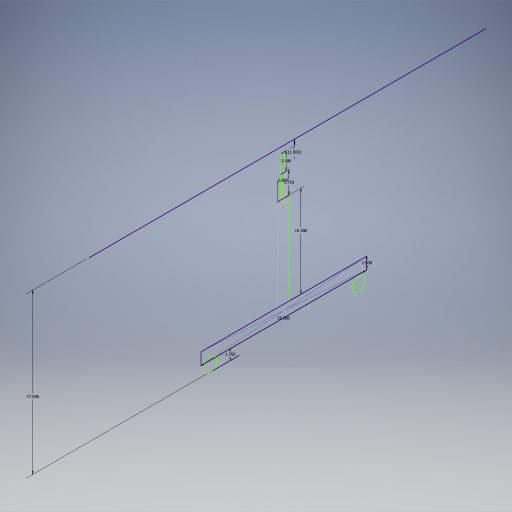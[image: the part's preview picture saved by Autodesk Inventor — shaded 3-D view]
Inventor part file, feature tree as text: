
AUTODESK INVENTOR PART (.ipt)
format: ipt  version: 2024.2 (Build 282272000, 272)  size: 275,456 bytes
history: native  units: in
note: dims shown in document units (in); Inventor stores cm internally (conversion verified against a paired STEP export)
features: sketch x1
ambient origin geometry x8: Origin, YZ Plane, XZ Plane, XY Plane, X Axis, Y Axis, Z Axis, Center Point
feature tree (1):
  sketch  "Sketch1"  dims[d0=2.0in d1=28.0in d2=2.0in d3=15.5in d4=1.75in d5=27.0in d7=3.75in d8=3.0in d10=1.0in]
